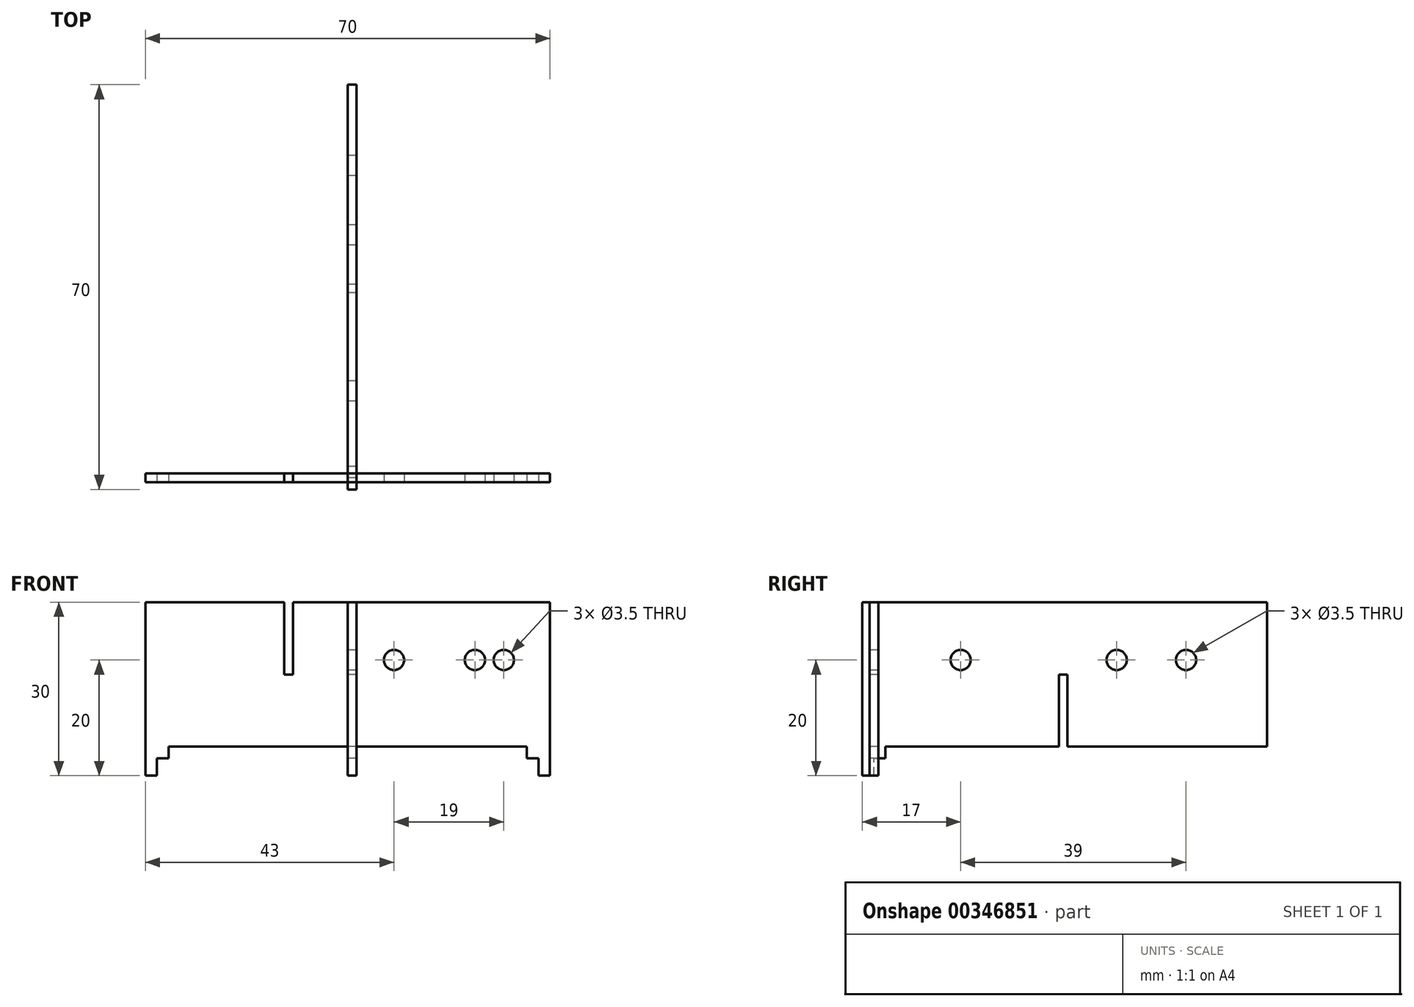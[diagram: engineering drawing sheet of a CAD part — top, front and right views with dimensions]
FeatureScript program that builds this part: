
annotation { "Feature Type Name" : "Feature", "Feature Type Description" : "" }
export const myFeature = defineFeature(function(context is Context, id is Id, definition is map)
    precondition{}
    {
        {
            var Q0;
            Q0=qCreatedBy(makeId("Front.planeOp"),FACE);
            var sketch = newSketch(context, id + "F0", { "sketchPlane" : qUnion([Q0])});
            skLineSegment(sketch, "E0.left", {"start": v(-35, 27) * mm, "end": v(-35, -3) * mm});
            skLineSegment(sketch, "E0.right", {"start": v(35, 27) * mm, "end": v(35, -3) * mm});
            skLineSegment(sketch, "E1", {"start": v(35, -3) * mm, "end": v(33, -3) * mm});
            skLineSegment(sketch, "E2", {"start": v(33, -3) * mm, "end": v(33, 0) * mm});
            skLineSegment(sketch, "E3", {"start": v(33, 0) * mm, "end": v(31, 0) * mm});
            skLineSegment(sketch, "E4", {"start": v(31, 0) * mm, "end": v(31, 2) * mm});
            skLineSegment(sketch, "E5", {"start": v(31, 2) * mm, "end": v(-31, 2) * mm});
            skLineSegment(sketch, "E6", {"start": v(-31, 2) * mm, "end": v(-31, 0) * mm});
            skLineSegment(sketch, "E7", {"start": v(-31, 0) * mm, "end": v(-33, 0) * mm});
            skLineSegment(sketch, "E8", {"start": v(-33, 0) * mm, "end": v(-33, -3) * mm});
            skLineSegment(sketch, "E9", {"start": v(-33, -3) * mm, "end": v(-35, -3) * mm});
            skCircle(sketch, "E10", {"center": v(27, 17) * mm, "radius": 1.75 * mm});
            skCircle(sketch, "E11", {"center": v(22, 17) * mm, "radius": 1.75 * mm});
            skCircle(sketch, "E12", {"center": v(8, 17) * mm, "radius": 1.75 * mm});
            skLineSegment(sketch, "E13", {"start": v(-11, 27) * mm, "end": v(-11, 14.5) * mm});
            skLineSegment(sketch, "E14", {"start": v(-11, 14.5) * mm, "end": v(-9.5, 14.5) * mm});
            skLineSegment(sketch, "E15", {"start": v(-9.5, 14.5) * mm, "end": v(-9.5, 27) * mm});
            skLineSegment(sketch, "E16", {"start": v(-11, 27) * mm, "end": v(-35, 27) * mm});
            skLineSegment(sketch, "E17", {"start": v(-9.5, 27) * mm, "end": v(35, 27) * mm});
            skSolve(sketch);
        }
        {
            var Q0;
            Q0 = qSketchRegion(id + "F0", true);
            extrude(context, id + "F1", {"entities" : qUnion([Q0]), "endBound" : BoundingType.SYMMETRIC, "oppositeDirection" : true, "depth" : 1.5 * mm});
        }
        {
            var Q0;
            Q0=qCreatedBy(makeId("Right.planeOp"),FACE);
            var sketch = newSketch(context, id + "F2", { "sketchPlane" : qUnion([Q0])});
            skLineSegment(sketch, "E18", {"start": v(0.75, 27) * mm, "end": v(68, 27) * mm});
            skLineSegment(sketch, "E19", {"start": v(68, 27) * mm, "end": v(-2, 27) * mm});
            skLineSegment(sketch, "E20", {"start": v(-2, 27) * mm, "end": v(-2, -3) * mm});
            skLineSegment(sketch, "E21", {"start": v(-2, -3) * mm, "end": v(0, -3) * mm});
            skLineSegment(sketch, "E22", {"start": v(0, -3) * mm, "end": v(0, 0) * mm});
            skLineSegment(sketch, "E23", {"start": v(0, 0) * mm, "end": v(2, 0) * mm});
            skLineSegment(sketch, "E24", {"start": v(2, 0) * mm, "end": v(2, 2) * mm});
            skLineSegment(sketch, "E25", {"start": v(32, 2) * mm, "end": v(32, 14.5) * mm});
            skLineSegment(sketch, "E26", {"start": v(32, 14.5) * mm, "end": v(33.5, 14.5) * mm});
            skLineSegment(sketch, "E27", {"start": v(33.5, 14.5) * mm, "end": v(33.5, 2) * mm});
            skLineSegment(sketch, "E28", {"start": v(32, 2) * mm, "end": v(2, 2) * mm});
            skLineSegment(sketch, "E29", {"start": v(33.5, 2) * mm, "end": v(68, 2) * mm});
            skCircle(sketch, "E30", {"center": v(15, 17) * mm, "radius": 1.75 * mm});
            skCircle(sketch, "E31", {"center": v(42, 17) * mm, "radius": 1.75 * mm});
            skCircle(sketch, "E32", {"center": v(54, 17) * mm, "radius": 1.75 * mm});
            skLineSegment(sketch, "E33", {"start": v(68, 27) * mm, "end": v(68, 2) * mm});
            skSolve(sketch);
        }
        {
            var Q0;
            Q0 = qSketchRegion(id + "F2", true);
            extrude(context, id + "F3", {"entities" : qUnion([Q0]), "depth" : 1.5 * mm});
        }
    });
